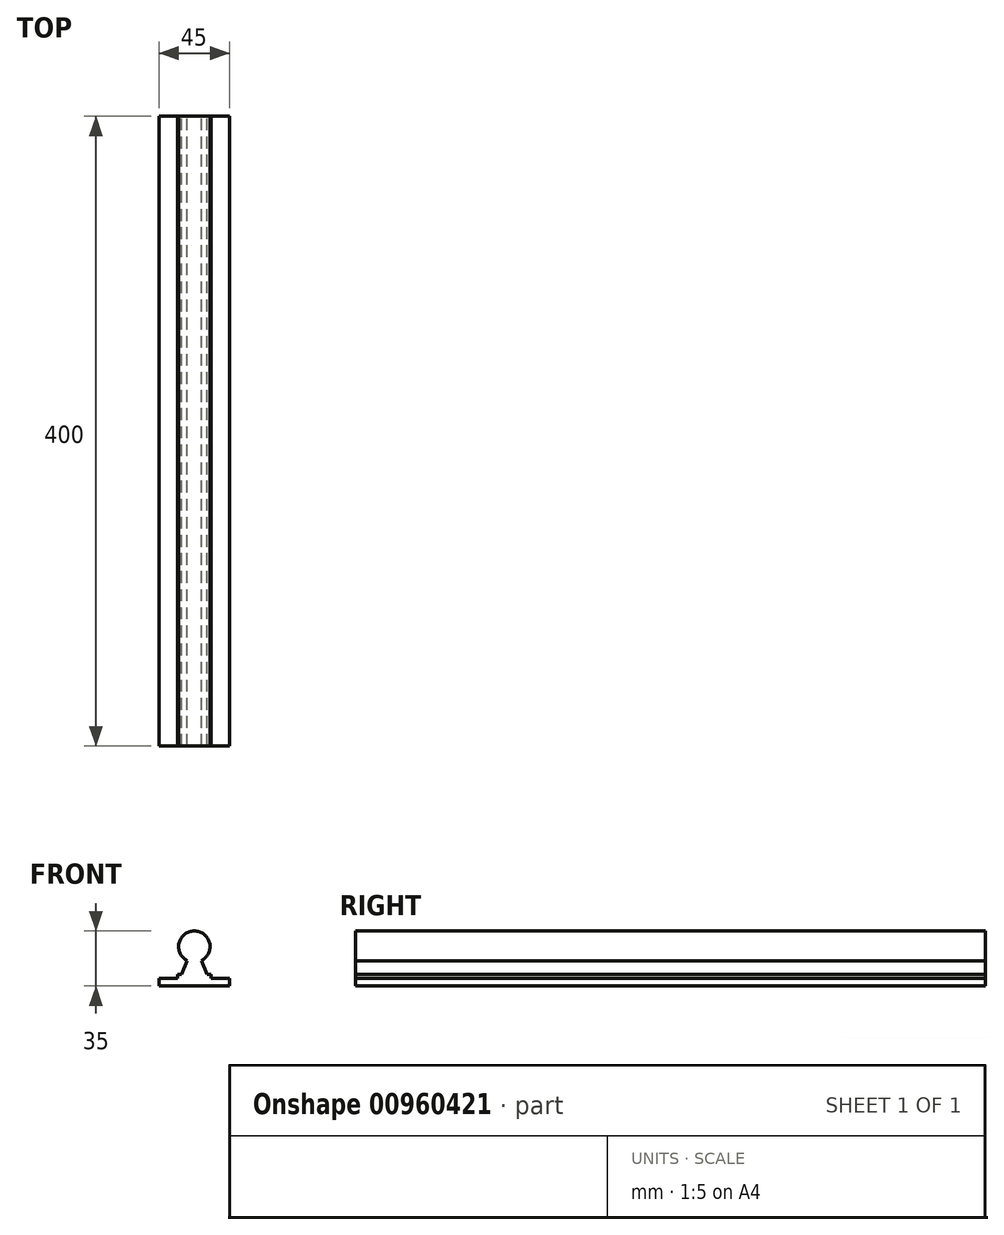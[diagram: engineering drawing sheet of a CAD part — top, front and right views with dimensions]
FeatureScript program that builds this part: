
annotation { "Feature Type Name" : "Feature", "Feature Type Description" : "" }
export const myFeature = defineFeature(function(context is Context, id is Id, definition is map)
    precondition{}
    {
        {
            var Q0;
            Q0=qCreatedBy(makeId("Front.planeOp"),FACE);
            var sketch = newSketch(context, id + "F0", { "sketchPlane" : qUnion([Q0])});
            skCircle(sketch, "E0", {"center": v(0, 0) * mm, "radius": 10 * mm});
            skLineSegment(sketch, "E1", {"start": v(-22.5, -25) * mm, "end": v(22.5, -25) * mm});
            skPoint(sketch, "E2", {"position": v(0, -25) * mm});
            skLineSegment(sketch, "E3", {"start": v(-22.5, -25) * mm, "end": v(-22.5, -20) * mm});
            skLineSegment(sketch, "E4", {"start": v(-22.5, -20) * mm, "end": v(-10.5, -20) * mm});
            skLineSegment(sketch, "E5", {"start": v(-10.5, -20) * mm, "end": v(-10.5, -17.5) * mm});
            skLineSegment(sketch, "E6", {"start": v(-10.5, -17.5) * mm, "end": v(-8, -17.5) * mm});
            skLineSegment(sketch, "E7", {"start": v(-8, -17.5) * mm, "end": v(-4.5, -8.93) * mm});
            skLineSegment(sketch, "E8", {"start": v(0, -29.05) * mm, "end": v(0, 13.28) * mm, "construction": true});
            skLineSegment(sketch, "E9.MirrorCS", {"start": v(8, -17.5) * mm, "end": v(4.5, -8.93) * mm});
            skLineSegment(sketch, "E10.MirrorCS", {"start": v(10.5, -17.5) * mm, "end": v(8, -17.5) * mm});
            skLineSegment(sketch, "E11.MirrorCS", {"start": v(10.5, -20) * mm, "end": v(10.5, -17.5) * mm});
            skLineSegment(sketch, "E12.MirrorCS", {"start": v(22.5, -20) * mm, "end": v(10.5, -20) * mm});
            skLineSegment(sketch, "E13.MirrorCS", {"start": v(22.5, -25) * mm, "end": v(22.5, -20) * mm});
            skSolve(sketch);
        }
        {
            var Q0;
            Q0=qSketchRegion(id+"F0",true);
            extrude(context, id + "F1", {"entities" : qUnion([Q0]), "depth" : 400 * mm, "offsetDistance" : 25 * mm});
        }
    });
